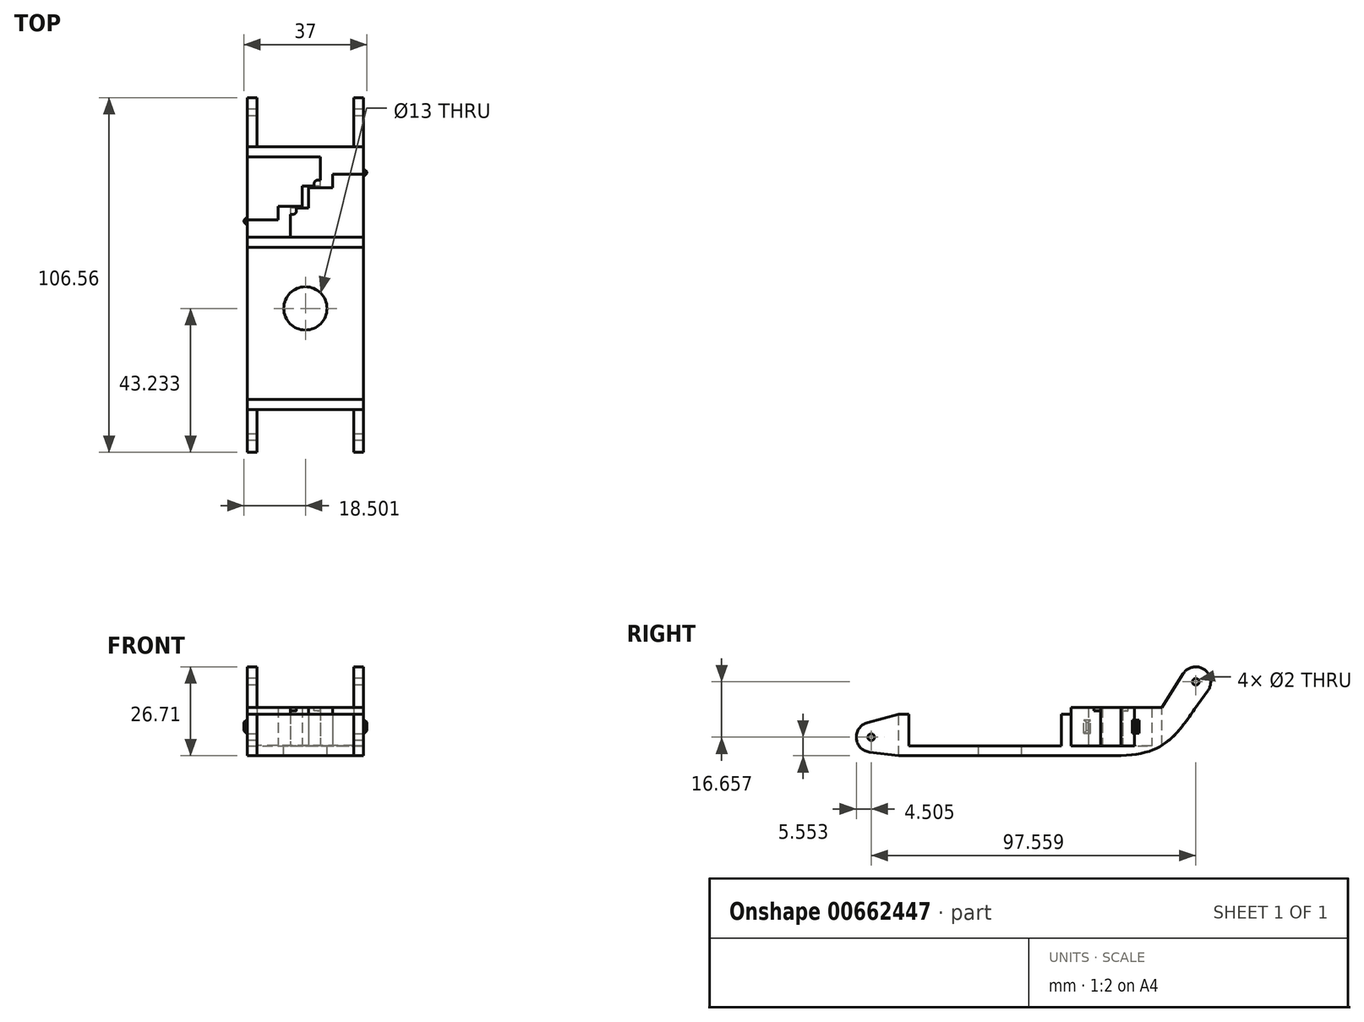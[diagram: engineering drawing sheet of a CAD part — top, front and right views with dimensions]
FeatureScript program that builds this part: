
annotation { "Feature Type Name" : "Feature", "Feature Type Description" : "" }
export const myFeature = defineFeature(function(context is Context, id is Id, definition is map)
    precondition{}
    {
        {
            var Q0;
            Q0=qCreatedBy(makeId("Top.planeOp"),FACE);
            var sketch = newSketch(context, id + "F0", { "sketchPlane" : qUnion([Q0])});
            skLineSegment(sketch, "E0.bottom", {"start": v(-9.64, 16.1) * mm, "end": v(7.86, 16.1) * mm});
            skLineSegment(sketch, "E0.top", {"start": v(-9.64, -29.7) * mm, "end": v(25.36, -29.7) * mm});
            skLineSegment(sketch, "E0.left", {"start": v(-9.64, 16.1) * mm, "end": v(-9.64, -29.7) * mm});
            skLineSegment(sketch, "E1", {"start": v(7.86, 16.1) * mm, "end": v(25.36, 16.1) * mm});
            skCircle(sketch, "E2", {"center": v(7.86, -2.29) * mm, "radius": 6.5 * mm});
            skLineSegment(sketch, "E3.MirrorCS", {"start": v(-9.64, 43.3) * mm, "end": v(-6.47, 43.3) * mm});
            skLineSegment(sketch, "E4.MirrorCS", {"start": v(7.86, 27.9) * mm, "end": v(7.86, 34.5) * mm});
            skLineSegment(sketch, "E5.MirrorCS", {"start": v(-9.64, 24.3) * mm, "end": v(-0.34, 24.3) * mm});
            skLineSegment(sketch, "E6.MirrorCS", {"start": v(12.36, 35.3) * mm, "end": v(12.36, 43.3) * mm});
            skLineSegment(sketch, "E7.MirrorCS", {"start": v(-6.47, 43.3) * mm, "end": v(12.36, 43.3) * mm});
            skLineSegment(sketch, "E8.MirrorCS", {"start": v(-9.64, 24.3) * mm, "end": v(-9.64, 43.3) * mm});
            skPoint(sketch, "E9", {"position": v(7.86, 31.6) * mm});
            skLineSegment(sketch, "E10", {"start": v(-9.64, 16.1) * mm, "end": v(-9.64, 19.1) * mm});
            skLineSegment(sketch, "E11", {"start": v(-9.64, 19.1) * mm, "end": v(25.36, 19.1) * mm});
            skLineSegment(sketch, "E12", {"start": v(-9.64, -29.7) * mm, "end": v(-9.64, -32.7) * mm});
            skLineSegment(sketch, "E13", {"start": v(-9.64, -32.7) * mm, "end": v(25.36, -32.7) * mm});
            skLineSegment(sketch, "E14", {"start": v(25.36, -32.7) * mm, "end": v(25.36, -29.7) * mm});
            skLineSegment(sketch, "E15", {"start": v(25.36, 19.1) * mm, "end": v(25.36, 19.1) * mm});
            skLineSegment(sketch, "E16", {"start": v(25.36, 19.1) * mm, "end": v(25.36, -29.7) * mm});
            skLineSegment(sketch, "E17.MirrorCS", {"start": v(25.36, 19.1) * mm, "end": v(22.2, 19.1) * mm});
            skLineSegment(sketch, "E18.MirrorCS", {"start": v(7.86, 34.5) * mm, "end": v(7.86, 27.9) * mm});
            skLineSegment(sketch, "E19.MirrorCS", {"start": v(25.36, 38.1) * mm, "end": v(16.06, 38.1) * mm});
            skLineSegment(sketch, "E20.MirrorCS", {"start": v(3.36, 27.1) * mm, "end": v(3.36, 19.1) * mm});
            skLineSegment(sketch, "E21.MirrorCS", {"start": v(22.2, 19.1) * mm, "end": v(3.36, 19.1) * mm});
            skLineSegment(sketch, "E22.MirrorCS", {"start": v(25.36, 38.1) * mm, "end": v(25.36, 19.1) * mm});
            skPoint(sketch, "E23", {"position": v(7.86, 30.8) * mm});
            skLineSegment(sketch, "E24", {"start": v(-9.64, 19.1) * mm, "end": v(-9.64, 24.3) * mm});
            skLineSegment(sketch, "E25", {"start": v(12.36, 43.3) * mm, "end": v(25.36, 43.3) * mm});
            skLineSegment(sketch, "E26", {"start": v(25.36, 43.3) * mm, "end": v(25.36, 38.1) * mm});
            skLineSegment(sketch, "E27", {"start": v(-9.64, 43.3) * mm, "end": v(-9.64, 46.3) * mm});
            skLineSegment(sketch, "E28", {"start": v(-9.64, 46.3) * mm, "end": v(25.36, 46.3) * mm});
            skLineSegment(sketch, "E29", {"start": v(25.36, 46.3) * mm, "end": v(25.36, 43.3) * mm});
            skLineSegment(sketch, "E30", {"start": v(25.36, -29.4) * mm, "end": v(-9.64, -29.4) * mm});
            skLineSegment(sketch, "E31", {"start": v(16.06, 38.1) * mm, "end": v(16.06, 34) * mm});
            skLineSegment(sketch, "E32", {"start": v(16.06, 34) * mm, "end": v(7.86, 34) * mm});
            skLineSegment(sketch, "E33", {"start": v(7.86, 34.5) * mm, "end": v(12.36, 34.5) * mm});
            skLineSegment(sketch, "E34", {"start": v(12.36, 34.5) * mm, "end": v(12.36, 35.3) * mm});
            skLineSegment(sketch, "E35", {"start": v(-0.34, 24.3) * mm, "end": v(-0.34, 28.4) * mm});
            skLineSegment(sketch, "E36", {"start": v(7.86, 27.9) * mm, "end": v(3.36, 27.9) * mm});
            skLineSegment(sketch, "E37", {"start": v(3.36, 27.9) * mm, "end": v(3.36, 27.1) * mm});
            skLineSegment(sketch, "E38", {"start": v(7.86, 34.5) * mm, "end": v(6.93, 34.5) * mm});
            skLineSegment(sketch, "E39", {"start": v(7.86, 27.9) * mm, "end": v(8.8, 27.9) * mm});
            skLineSegment(sketch, "E40", {"start": v(6.93, 34.5) * mm, "end": v(6.93, 28.4) * mm});
            skLineSegment(sketch, "E41", {"start": v(8.8, 27.9) * mm, "end": v(8.8, 34) * mm});
            skLineSegment(sketch, "E42", {"start": v(-0.34, 28.4) * mm, "end": v(7.86, 28.4) * mm});
            skSolve(sketch);
        }
        {
            var Q0;
            {var subQ2=sQuery(id+"F0.wireOp",EDGE,"E0.bottom");Q0=makeQuery(id+"F0.imprint","IMPRINT",FACE,{"disambiguationData":[TD([[makeQuery(id+"F0.imprint","IMPRINT",EDGE,{"derivedFrom":subQ2}),-1.0]])]});}
            var Q1;
            Q1=makeQuery(id+"F0.imprint","IMPRINT",FACE,{"disambiguationData":[TD([[makeQuery(id+"F0.imprint","IMPRINT",EDGE,{"derivedFrom":sQuery(id+"F0.wireOp",EDGE,"E0.top")}),-1.0]])]});
            var Q2;
            Q2=makeQuery(id+"F0.imprint","IMPRINT",FACE,{"disambiguationData":[TD([[makeQuery(id+"F0.imprint","IMPRINT",EDGE,{"derivedFrom":sQuery(id+"F0.wireOp",EDGE,"E0.bottom")}),1.0]])]});
            var Q3;
            {var subQ1=sQuery(id+"F0.wireOp",EDGE,"65957815-49e4-4ce0-b1aa-900a07c07509.MirrorCS");Q3=makeQuery(id+"F0.imprint","IMPRINT",FACE,{"disambiguationData":[TD([[makeQuery(id+"F0.imprint","IMPRINT",EDGE,{"derivedFrom":subQ1}),-1.0]])]});}
            var Q4;
            Q4=makeQuery(id+"F0.imprint","IMPRINT",FACE,{"disambiguationData":[TD([[makeQuery(id+"F0.imprint","IMPRINT",EDGE,{"derivedFrom":sQuery(id+"F0.wireOp",EDGE,"793e653a-9070-4513-9301-6aa9de76053a.MirrorCS")}),-1.0]])]});
            var Q5;
            {var subQ3=sQuery(id+"F0.wireOp",EDGE,"bcf4ff58-2fc9-42ac-b040-1ddef6c83d7c.MirrorCS");Q5=makeQuery(id+"F0.imprint","IMPRINT",FACE,{"disambiguationData":[TD([[makeQuery(id+"F0.imprint","IMPRINT",EDGE,{"derivedFrom":subQ3}),1.0]])]});}
            var Q6;
            Q6=makeQuery(id+"F0.imprint","IMPRINT",FACE,{"disambiguationData":[TD([[makeQuery(id+"F0.imprint","IMPRINT",EDGE,{"derivedFrom":sQuery(id+"F0.wireOp",EDGE,"793e653a-9070-4513-9301-6aa9de76053a.MirrorCS")}),1.0]])]});
            var Q7;
            Q7=makeQuery(id+"F0.imprint","IMPRINT",FACE,{"disambiguationData":[TD([[makeQuery(id+"F0.imprint","IMPRINT",EDGE,{"derivedFrom":sQuery(id+"F0.wireOp",EDGE,"E3.MirrorCS")}),1.0]])]});
            var Q8;
            {var subQ0=sQuery(id+"F0.wireOp",EDGE,"E0.top");Q8=makeQuery(id+"F0.imprint","IMPRINT",FACE,{"disambiguationData":[TD([[makeQuery(id+"F0.imprint","IMPRINT",EDGE,{"derivedFrom":subQ0}),1.0]])]});}
            var Q9;
            Q9=makeQuery(id+"F0.imprint","IMPRINT",FACE,{"disambiguationData":[TD([[makeQuery(id+"F0.imprint","IMPRINT",EDGE,{"derivedFrom":sQuery(id+"F0.wireOp",EDGE,"E6.MirrorCS")}),-1.0]])]});
            var Q10;
            Q10=makeQuery(id+"F0.imprint","IMPRINT",FACE,{"disambiguationData":[TD([[makeQuery(id+"F0.imprint","IMPRINT",EDGE,{"derivedFrom":sQuery(id+"F0.wireOp",EDGE,"E5.MirrorCS")}),-1.0]])]});
            var Q11;
            {var subQ3=sQuery(id+"F0.wireOp",EDGE,"E38");Q11=makeQuery(id+"F0.imprint","IMPRINT",FACE,{"disambiguationData":[TD([[makeQuery(id+"F0.imprint","IMPRINT",EDGE,{"derivedFrom":subQ3}),1.0]])]});}
            var Q12;
            {var subQ0=sQuery(id+"F0.wireOp",EDGE,"E39");Q12=makeQuery(id+"F0.imprint","IMPRINT",FACE,{"disambiguationData":[TD([[makeQuery(id+"F0.imprint","IMPRINT",EDGE,{"derivedFrom":subQ0}),1.0]])]});}
            var Q13;
            Q13=makeQuery(id+"F0.imprint","IMPRINT",FACE,{"disambiguationData":[TD([[makeQuery(id+"F0.imprint","IMPRINT",EDGE,{"derivedFrom":sQuery(id+"F0.wireOp",EDGE,"E3.MirrorCS")}),-1.0]])]});
            var Q14;
            Q14=makeQuery(id+"F0.imprint","IMPRINT",FACE,{"disambiguationData":[TD([[makeQuery(id+"F0.imprint","IMPRINT",EDGE,{"derivedFrom":sQuery(id+"F0.wireOp",EDGE,"E19.MirrorCS")}),1.0]])]});
            extrude(context, id + "F1", {"entities" : qUnion([Q0, Q1, Q2, Q3, Q4, Q5, Q6, Q7, Q8, Q9, Q10, Q11, Q12, Q13, Q14]), "oppositeDirection" : true, "depth" : 3 * mm, "offsetDistance" : 25 * mm});
        }
        {
            var Q0;
            Q0=makeQuery(id+"F0.imprint","IMPRINT",FACE,{"disambiguationData":[TD([[makeQuery(id+"F0.imprint","IMPRINT",EDGE,{"derivedFrom":sQuery(id+"F0.wireOp",EDGE,"E0.top")}),-1.0]])]});
            var Q1;
            Q1=makeQuery(id+"F0.imprint","IMPRINT",FACE,{"disambiguationData":[TD([[makeQuery(id+"F0.imprint","IMPRINT",EDGE,{"derivedFrom":sQuery(id+"F0.wireOp",EDGE,"E0.bottom")}),1.0]])]});
            extrude(context, id + "F2", {"entities" : qUnion([Q0, Q1]), "operationType" : NewBodyOperationType.ADD, "depth" : 9.5 * mm, "offsetDistance" : 25 * mm});
        }
        {
            var Q0;
            {var subQ1=sQuery(id+"F0.wireOp",EDGE,"65957815-49e4-4ce0-b1aa-900a07c07509.MirrorCS");Q0=makeQuery(id+"F0.imprint","IMPRINT",FACE,{"disambiguationData":[TD([[makeQuery(id+"F0.imprint","IMPRINT",EDGE,{"derivedFrom":subQ1}),-1.0]])]});}
            var Q1;
            Q1=makeQuery(id+"F0.imprint","IMPRINT",FACE,{"disambiguationData":[TD([[makeQuery(id+"F0.imprint","IMPRINT",EDGE,{"derivedFrom":sQuery(id+"F0.wireOp",EDGE,"793e653a-9070-4513-9301-6aa9de76053a.MirrorCS")}),-1.0]])]});
            var Q2;
            Q2=makeQuery(id+"F0.imprint","IMPRINT",FACE,{"disambiguationData":[TD([[makeQuery(id+"F0.imprint","IMPRINT",EDGE,{"derivedFrom":sQuery(id+"F0.wireOp",EDGE,"E3.MirrorCS")}),1.0]])]});
            var Q3;
            Q3=makeQuery(id+"F0.imprint","IMPRINT",FACE,{"disambiguationData":[TD([[makeQuery(id+"F0.imprint","IMPRINT",EDGE,{"derivedFrom":sQuery(id+"F0.wireOp",EDGE,"E5.MirrorCS")}),-1.0]])]});
            var Q4;
            {var subQ0=sQuery(id+"F0.wireOp",EDGE,"E39");Q4=makeQuery(id+"F0.imprint","IMPRINT",FACE,{"disambiguationData":[TD([[makeQuery(id+"F0.imprint","IMPRINT",EDGE,{"derivedFrom":subQ0}),1.0]])]});}
            var Q5;
            {var subQ3=sQuery(id+"F0.wireOp",EDGE,"E38");Q5=makeQuery(id+"F0.imprint","IMPRINT",FACE,{"disambiguationData":[TD([[makeQuery(id+"F0.imprint","IMPRINT",EDGE,{"derivedFrom":subQ3}),1.0]])]});}
            var Q6;
            Q6=makeQuery(id+"F0.imprint","IMPRINT",FACE,{"disambiguationData":[TD([[makeQuery(id+"F0.imprint","IMPRINT",EDGE,{"derivedFrom":sQuery(id+"F0.wireOp",EDGE,"E6.MirrorCS")}),-1.0]])]});
            extrude(context, id + "F3", {"entities" : qUnion([Q0, Q1, Q2, Q3, Q4, Q5, Q6]), "operationType" : NewBodyOperationType.ADD, "depth" : 11.5 * mm, "offsetDistance" : 25 * mm});
        }
        {
            var Q0;
            {var subQ0=sQuery(id+"F0.wireOp",EDGE,"E29");var subQ1=sQuery(id+"F0.wireOp",EDGE,"E26");var subQ2=sQuery(id+"F0.wireOp",EDGE,"E16");var subQ3=sQuery(id+"F0.wireOp",EDGE,"E14");Q0=makeQuery(id+"F3.boolean.opBoolean","MERGE",FACE,{"derivedFrom":[makeQuery(id+"F2.boolean.opBoolean","MERGE",FACE,{"derivedFrom":[makeQuery(id+"F1.opExtrude","SWEPT_FACE",FACE,{"disambiguationData":[OSD([subQ3,subQ2,sQuery(id+"F0.wireOp",EDGE,"E22.MirrorCS"),subQ1,subQ0])]}),makeQuery(id+"F2.opExtrude","SWEPT_FACE",FACE,{"disambiguationData":[OSD([subQ3])]}),makeQuery(id+"F2.opExtrude","SWEPT_FACE",FACE,{"disambiguationData":[OSD([subQ2])]})]}),makeQuery(id+"F3.opExtrude","SWEPT_FACE",FACE,{"disambiguationData":[OSD([subQ1,subQ0])]})]});}
            var sketch = newSketch(context, id + "F4", { "sketchPlane" : qUnion([Q0])});
            skLineSegment(sketch, "E43.6", {"start": v(46.3, -3) * mm, "end": v(46.3, 11.5) * mm});
            skLineSegment(sketch, "E43.7", {"start": v(46.3, 11.5) * mm, "end": v(38.1, 11.5) * mm});
            skLineSegment(sketch, "E43.8", {"start": v(-32.7, -3) * mm, "end": v(-32.7, 9.5) * mm});
            skCircle(sketch, "E44", {"center": v(56.54, 19.2) * mm, "radius": 4.5 * mm});
            skLineSegment(sketch, "E45", {"start": v(46.3, -3) * mm, "end": v(60.21, 16.6) * mm});
            skLineSegment(sketch, "E46", {"start": v(46.3, 11.5) * mm, "end": v(52.75, 21.63) * mm});
            skCircle(sketch, "E47", {"center": v(-41.02, 2.55) * mm, "radius": 4.5 * mm});
            skLineSegment(sketch, "E48", {"start": v(-32.7, 9.5) * mm, "end": v(-42.2, 6.9) * mm});
            skLineSegment(sketch, "E49", {"start": v(-32.7, -3) * mm, "end": v(-41.56, -1.91) * mm});
            skSolve(sketch);
        }
        {
            var Q0;
            {var subQ0=sQuery(id+"F4.wireOp",EDGE,"E47");var subQ1=makeQuery(id+"F4.imprint","INTERSECT",VERTEX,{"derivedFrom":[subQ0,sQuery(id+"F4.wireOp",EDGE,"PAik2qhj-YHKu-fe6H-CUS2-yW6YpYjkYPtX")]});Q0=makeQuery(id+"F4.imprint","IMPRINT",FACE,{"disambiguationData":[TD([[makeQuery(id+"F4.imprint","IMPRINT",EDGE,{"disambiguationData":[TD([[subQ1,1.0]])],"derivedFrom":subQ0}),1.0]])]});}
            var Q1;
            Q1=makeQuery(id+"F4.imprint","IMPRINT",FACE,{"disambiguationData":[TD([[makeQuery(id+"F4.imprint","IMPRINT",EDGE,{"derivedFrom":sQuery(id+"F4.wireOp",EDGE,"E43.8")}),1.0]])]});
            var Q2;
            Q2=makeQuery(id+"F4.imprint","IMPRINT",FACE,{"disambiguationData":[TD([[makeQuery(id+"F4.imprint","IMPRINT",EDGE,{"derivedFrom":sQuery(id+"F4.wireOp",EDGE,"E43.6")}),-1.0]])]});
            var Q3;
            {var subQ0=sQuery(id+"F4.wireOp",EDGE,"E44");var subQ1=makeQuery(id+"F4.imprint","INTERSECT",VERTEX,{"derivedFrom":[subQ0,sQuery(id+"F4.wireOp",EDGE,"E45")]});Q3=makeQuery(id+"F4.imprint","IMPRINT",FACE,{"disambiguationData":[TD([[makeQuery(id+"F4.imprint","IMPRINT",EDGE,{"disambiguationData":[TD([[subQ1,1.0]])],"derivedFrom":subQ0}),1.0]])]});}
            extrude(context, id + "F5", {"entities" : qUnion([Q0, Q1, Q2, Q3]), "operationType" : NewBodyOperationType.ADD, "oppositeDirection" : true, "depth" : 3 * mm, "offsetDistance" : 25 * mm});
        }
        {
            var Q0;
            {var subQ0=sQuery(id+"F0.wireOp",EDGE,"E27");var subQ1=sQuery(id+"F0.wireOp",EDGE,"E24");var subQ2=sQuery(id+"F0.wireOp",EDGE,"E12");var subQ3=sQuery(id+"F0.wireOp",EDGE,"E10");Q0=makeQuery(id+"F3.boolean.opBoolean","MERGE",FACE,{"derivedFrom":[makeQuery(id+"F2.boolean.opBoolean","MERGE",FACE,{"derivedFrom":[makeQuery(id+"F1.opExtrude","SWEPT_FACE",FACE,{"disambiguationData":[OSD([sQuery(id+"F0.wireOp",EDGE,"E0.left"),sQuery(id+"F0.wireOp",EDGE,"E8.MirrorCS"),subQ3,subQ2,subQ1,subQ0])]}),makeQuery(id+"F2.opExtrude","SWEPT_FACE",FACE,{"disambiguationData":[OSD([subQ3])]}),makeQuery(id+"F2.opExtrude","SWEPT_FACE",FACE,{"disambiguationData":[OSD([subQ2])]})]}),makeQuery(id+"F3.opExtrude","SWEPT_FACE",FACE,{"disambiguationData":[OSD([subQ1])]}),makeQuery(id+"F3.opExtrude","SWEPT_FACE",FACE,{"disambiguationData":[OSD([subQ0])]})]});}
            var sketch = newSketch(context, id + "F6", { "sketchPlane" : qUnion([Q0])});
            skLineSegment(sketch, "E50.0", {"start": v(-46.3, -3) * mm, "end": v(-60.21, 16.6) * mm});
            skArc(sketch, "E50.1", {"start": v(-60.21, 16.6) * mm, "mid": v(-59.06, 22.94) * mm, "end": v(-52.75, 21.63) * mm});
            skLineSegment(sketch, "E50.2", {"start": v(-46.3, 11.5) * mm, "end": v(-52.75, 21.63) * mm});
            skLineSegment(sketch, "E50.3", {"start": v(-46.3, -3) * mm, "end": v(-46.3, 11.5) * mm});
            skLineSegment(sketch, "E50.4", {"start": v(32.7, -3) * mm, "end": v(32.7, 9.5) * mm});
            skLineSegment(sketch, "E50.5", {"start": v(32.7, 9.5) * mm, "end": v(42.2, 6.9) * mm});
            skArc(sketch, "E50.6", {"start": v(42.2, 6.9) * mm, "mid": v(45.5, 2.23) * mm, "end": v(41.56, -1.91) * mm});
            skLineSegment(sketch, "E50.7", {"start": v(32.7, -3) * mm, "end": v(41.56, -1.91) * mm});
            skSolve(sketch);
        }
        {
            var Q0;
            Q0=makeQuery(id+"F6.imprint","IMPRINT",FACE,{"disambiguationData":[TD([[makeQuery(id+"F6.imprint","IMPRINT",EDGE,{"derivedFrom":sQuery(id+"F6.wireOp",EDGE,"E50.0")}),-1.0]])]});
            var Q1;
            Q1=makeQuery(id+"F6.imprint","IMPRINT",FACE,{"disambiguationData":[TD([[makeQuery(id+"F6.imprint","IMPRINT",EDGE,{"derivedFrom":sQuery(id+"F6.wireOp",EDGE,"E50.4")}),-1.0]])]});
            extrude(context, id + "F7", {"entities" : qUnion([Q0, Q1]), "operationType" : NewBodyOperationType.ADD, "oppositeDirection" : true, "depth" : 3 * mm, "offsetDistance" : 25 * mm});
        }
        {
            var Q0;
            {var subQ0=sQuery(id+"F0.wireOp",EDGE,"E27");var subQ1=sQuery(id+"F0.wireOp",EDGE,"E24");var subQ2=sQuery(id+"F0.wireOp",EDGE,"E12");var subQ3=sQuery(id+"F0.wireOp",EDGE,"E10");Q0=makeQuery(id+"F7.boolean.opBoolean","MERGE",FACE,{"derivedFrom":[makeQuery(id+"F3.boolean.opBoolean","MERGE",FACE,{"derivedFrom":[makeQuery(id+"F2.boolean.opBoolean","MERGE",FACE,{"derivedFrom":[makeQuery(id+"F1.opExtrude","SWEPT_FACE",FACE,{"disambiguationData":[OSD([sQuery(id+"F0.wireOp",EDGE,"E0.left"),sQuery(id+"F0.wireOp",EDGE,"E8.MirrorCS"),subQ3,subQ2,subQ1,subQ0])]}),makeQuery(id+"F2.opExtrude","SWEPT_FACE",FACE,{"disambiguationData":[OSD([subQ3])]}),makeQuery(id+"F2.opExtrude","SWEPT_FACE",FACE,{"disambiguationData":[OSD([subQ2])]})]}),makeQuery(id+"F3.opExtrude","SWEPT_FACE",FACE,{"disambiguationData":[OSD([subQ1])]}),makeQuery(id+"F3.opExtrude","SWEPT_FACE",FACE,{"disambiguationData":[OSD([subQ0])]})]}),makeQuery(id+"F7.opExtrude","CAP_FACE",FACE,{"disambiguationData":[OSD([sQuery(id+"F6.wireOp",EDGE,"E50.0"),sQuery(id+"F6.wireOp",EDGE,"E50.1"),sQuery(id+"F6.wireOp",EDGE,"E50.2"),sQuery(id+"F6.wireOp",EDGE,"E50.3")])],"isStart":true}),makeQuery(id+"F7.opExtrude","CAP_FACE",FACE,{"disambiguationData":[OSD([sQuery(id+"F6.wireOp",EDGE,"E50.4"),sQuery(id+"F6.wireOp",EDGE,"E50.5"),sQuery(id+"F6.wireOp",EDGE,"E50.6"),sQuery(id+"F6.wireOp",EDGE,"E50.7")])],"isStart":true})]});}
            var sketch = newSketch(context, id + "F8", { "sketchPlane" : qUnion([Q0])});
            skArc(sketch, "E51.0", {"start": v(-60.21, 16.6) * mm, "mid": v(-59.06, 22.94) * mm, "end": v(-52.75, 21.63) * mm});
            skArc(sketch, "E51.1", {"start": v(42.2, 6.9) * mm, "mid": v(45.5, 2.23) * mm, "end": v(41.56, -1.91) * mm});
            skCircle(sketch, "E52", {"center": v(-56.54, 19.2) * mm, "radius": 1 * mm});
            skCircle(sketch, "E53", {"center": v(41.02, 2.55) * mm, "radius": 1 * mm});
            skSolve(sketch);
        }
        {
            var Q0;
            Q0=makeQuery(id+"F8.imprint","IMPRINT",FACE,{"disambiguationData":[TD([[makeQuery(id+"F8.imprint","IMPRINT",EDGE,{"derivedFrom":sQuery(id+"F8.wireOp",EDGE,"E52")}),1.0]])]});
            var Q1;
            Q1=makeQuery(id+"F8.imprint","IMPRINT",FACE,{"disambiguationData":[TD([[makeQuery(id+"F8.imprint","IMPRINT",EDGE,{"derivedFrom":sQuery(id+"F8.wireOp",EDGE,"E53")}),1.0]])]});
            extrude(context, id + "F9", {"entities" : qUnion([Q0, Q1]), "operationType" : NewBodyOperationType.REMOVE, "endBound" : BoundingType.THROUGH_ALL, "oppositeDirection" : true, "depth" : 25 * mm, "offsetDistance" : 25 * mm});
        }
        {
            var Q0;
            {var subQ0=sQuery(id+"F0.wireOp",EDGE,"E29");var subQ1=sQuery(id+"F0.wireOp",EDGE,"E26");var subQ2=sQuery(id+"F0.wireOp",EDGE,"E16");var subQ3=sQuery(id+"F0.wireOp",EDGE,"E14");Q0=makeQuery(id+"F5.boolean.opBoolean","MERGE",FACE,{"derivedFrom":[makeQuery(id+"F3.boolean.opBoolean","MERGE",FACE,{"derivedFrom":[makeQuery(id+"F2.boolean.opBoolean","MERGE",FACE,{"derivedFrom":[makeQuery(id+"F1.opExtrude","SWEPT_FACE",FACE,{"disambiguationData":[OSD([subQ3,subQ2,sQuery(id+"F0.wireOp",EDGE,"E22.MirrorCS"),subQ1,subQ0])]}),makeQuery(id+"F2.opExtrude","SWEPT_FACE",FACE,{"disambiguationData":[OSD([subQ3])]}),makeQuery(id+"F2.opExtrude","SWEPT_FACE",FACE,{"disambiguationData":[OSD([subQ2])]})]}),makeQuery(id+"F3.opExtrude","SWEPT_FACE",FACE,{"disambiguationData":[OSD([subQ1,subQ0])]})]}),makeQuery(id+"F5.opExtrude","CAP_FACE",FACE,{"disambiguationData":[OSD([sQuery(id+"F4.wireOp",EDGE,"E43.6"),sQuery(id+"F4.wireOp",EDGE,"E44"),sQuery(id+"F4.wireOp",EDGE,"E45"),sQuery(id+"F4.wireOp",EDGE,"E46")])],"isStart":true}),makeQuery(id+"F5.opExtrude","CAP_FACE",FACE,{"disambiguationData":[OSD([sQuery(id+"F4.wireOp",EDGE,"E43.8"),sQuery(id+"F4.wireOp",EDGE,"E47"),sQuery(id+"F4.wireOp",EDGE,"E48"),sQuery(id+"F4.wireOp",EDGE,"E49")])],"isStart":true})]});}
            var sketch = newSketch(context, id + "F10", { "sketchPlane" : qUnion([Q0])});
            skLineSegment(sketch, "E54.0", {"start": v(38.1, 11.5) * mm, "end": v(38.1, 0) * mm});
            skPoint(sketch, "E55", {"position": v(38.1, 5.75) * mm});
            skLineSegment(sketch, "E56", {"start": v(35.03, 5.75) * mm, "end": v(42.1, 5.75) * mm, "construction": true});
            skLineSegment(sketch, "E57", {"start": v(37.5, 5.75) * mm, "end": v(37.5, 7.75) * mm});
            skLineSegment(sketch, "E58", {"start": v(37.5, 7.75) * mm, "end": v(39.5, 7.75) * mm});
            skLineSegment(sketch, "E59", {"start": v(39.5, 7.75) * mm, "end": v(39.5, 5.75) * mm});
            skLineSegment(sketch, "E60.MirrorCS", {"start": v(37.5, 3.75) * mm, "end": v(39.5, 3.75) * mm});
            skLineSegment(sketch, "E61.MirrorCS", {"start": v(37.5, 5.75) * mm, "end": v(37.5, 3.75) * mm});
            skLineSegment(sketch, "E62.MirrorCS", {"start": v(39.5, 3.75) * mm, "end": v(39.5, 5.75) * mm});
            skSolve(sketch);
        }
        {
            var Q0;
            {var subQ4=sQuery(id+"F10.wireOp",EDGE,"E59");Q0=makeQuery(id+"F10.imprint","IMPRINT",FACE,{"disambiguationData":[TD([[makeQuery(id+"F10.imprint","IMPRINT",EDGE,{"derivedFrom":subQ4}),-1.0]])]});}
            var Q1;
            {var subQ5=sQuery(id+"F10.wireOp",EDGE,"E57");Q1=makeQuery(id+"F10.imprint","IMPRINT",FACE,{"disambiguationData":[TD([[makeQuery(id+"F10.imprint","IMPRINT",EDGE,{"derivedFrom":subQ5}),-1.0]])]});}
            extrude(context, id + "F11", {"entities" : qUnion([Q0, Q1]), "operationType" : NewBodyOperationType.ADD, "depth" : 1 * mm, "offsetDistance" : 25 * mm});
        }
        {
            var Q0;
            {var subQ0=sQuery(id+"F0.wireOp",EDGE,"E27");var subQ1=sQuery(id+"F0.wireOp",EDGE,"E24");var subQ2=sQuery(id+"F0.wireOp",EDGE,"E12");var subQ3=sQuery(id+"F0.wireOp",EDGE,"E10");Q0=makeQuery(id+"F7.boolean.opBoolean","MERGE",FACE,{"derivedFrom":[makeQuery(id+"F3.boolean.opBoolean","MERGE",FACE,{"derivedFrom":[makeQuery(id+"F2.boolean.opBoolean","MERGE",FACE,{"derivedFrom":[makeQuery(id+"F1.opExtrude","SWEPT_FACE",FACE,{"disambiguationData":[OSD([sQuery(id+"F0.wireOp",EDGE,"E0.left"),sQuery(id+"F0.wireOp",EDGE,"E8.MirrorCS"),subQ3,subQ2,subQ1,subQ0])]}),makeQuery(id+"F2.opExtrude","SWEPT_FACE",FACE,{"disambiguationData":[OSD([subQ3])]}),makeQuery(id+"F2.opExtrude","SWEPT_FACE",FACE,{"disambiguationData":[OSD([subQ2])]})]}),makeQuery(id+"F3.opExtrude","SWEPT_FACE",FACE,{"disambiguationData":[OSD([subQ1])]}),makeQuery(id+"F3.opExtrude","SWEPT_FACE",FACE,{"disambiguationData":[OSD([subQ0])]})]}),makeQuery(id+"F7.opExtrude","CAP_FACE",FACE,{"disambiguationData":[OSD([sQuery(id+"F6.wireOp",EDGE,"E50.0"),sQuery(id+"F6.wireOp",EDGE,"E50.1"),sQuery(id+"F6.wireOp",EDGE,"E50.2"),sQuery(id+"F6.wireOp",EDGE,"E50.3")])],"isStart":true}),makeQuery(id+"F7.opExtrude","CAP_FACE",FACE,{"disambiguationData":[OSD([sQuery(id+"F6.wireOp",EDGE,"E50.4"),sQuery(id+"F6.wireOp",EDGE,"E50.5"),sQuery(id+"F6.wireOp",EDGE,"E50.6"),sQuery(id+"F6.wireOp",EDGE,"E50.7")])],"isStart":true})]});}
            var sketch = newSketch(context, id + "F12", { "sketchPlane" : qUnion([Q0])});
            skLineSegment(sketch, "E63", {"start": v(-24.3, 5.75) * mm, "end": v(-30.81, 5.75) * mm, "construction": true});
            skLineSegment(sketch, "E64", {"start": v(-24.9, 5.75) * mm, "end": v(-24.9, 7.75) * mm});
            skLineSegment(sketch, "E65", {"start": v(-24.9, 7.75) * mm, "end": v(-22.9, 7.75) * mm});
            skLineSegment(sketch, "E66", {"start": v(-22.9, 7.75) * mm, "end": v(-22.9, 5.75) * mm});
            skLineSegment(sketch, "E67.MirrorCS", {"start": v(-24.9, 5.75) * mm, "end": v(-24.9, 3.75) * mm});
            skLineSegment(sketch, "E68.MirrorCS", {"start": v(-22.9, 3.75) * mm, "end": v(-22.9, 5.75) * mm});
            skLineSegment(sketch, "E69.MirrorCS", {"start": v(-24.9, 3.75) * mm, "end": v(-22.9, 3.75) * mm});
            skSolve(sketch);
        }
        {
            var Q0;
            {var subQ1=sQuery(id+"F12.wireOp",EDGE,"E66");Q0=makeQuery(id+"F12.imprint","IMPRINT",FACE,{"disambiguationData":[TD([[makeQuery(id+"F12.imprint","IMPRINT",EDGE,{"derivedFrom":subQ1}),-1.0]])]});}
            var Q1;
            {var subQ5=sQuery(id+"F12.wireOp",EDGE,"E64");Q1=makeQuery(id+"F12.imprint","IMPRINT",FACE,{"disambiguationData":[TD([[makeQuery(id+"F12.imprint","IMPRINT",EDGE,{"derivedFrom":subQ5}),-1.0]])]});}
            extrude(context, id + "F13", {"entities" : qUnion([Q0, Q1]), "operationType" : NewBodyOperationType.ADD, "depth" : 1 * mm, "offsetDistance" : 25 * mm});
        }
        {
            var Q0;
            Q0=makeQuery(id+"F13.opExtrude","CAP_EDGE",EDGE,{"disambiguationData":[OSD([sQuery(id+"F12.wireOp",EDGE,"E64"),sQuery(id+"F12.wireOp",EDGE,"E67.MirrorCS")])],"isStart":false});
            var Q1;
            Q1=makeQuery(id+"F13.opExtrude","CAP_EDGE",EDGE,{"disambiguationData":[OSD([sQuery(id+"F12.wireOp",EDGE,"E66"),sQuery(id+"F12.wireOp",EDGE,"E68.MirrorCS")])],"isStart":false});
            var Q2;
            Q2=makeQuery(id+"F13.opExtrude","CAP_EDGE",EDGE,{"disambiguationData":[OSD([sQuery(id+"F12.wireOp",EDGE,"E65")])],"isStart":false});
            var Q3;
            Q3=makeQuery(id+"F13.opExtrude","CAP_EDGE",EDGE,{"disambiguationData":[OSD([sQuery(id+"F12.wireOp",EDGE,"E69.MirrorCS")])],"isStart":false});
            var Q4;
            Q4=makeQuery(id+"F11.opExtrude","CAP_EDGE",EDGE,{"disambiguationData":[OSD([sQuery(id+"F10.wireOp",EDGE,"E58")])],"isStart":false});
            var Q5;
            Q5=makeQuery(id+"F11.opExtrude","CAP_EDGE",EDGE,{"disambiguationData":[OSD([sQuery(id+"F10.wireOp",EDGE,"E57"),sQuery(id+"F10.wireOp",EDGE,"E61.MirrorCS")])],"isStart":false});
            var Q6;
            Q6=makeQuery(id+"F11.opExtrude","CAP_EDGE",EDGE,{"disambiguationData":[OSD([sQuery(id+"F10.wireOp",EDGE,"E60.MirrorCS")])],"isStart":false});
            var Q7;
            Q7=makeQuery(id+"F11.opExtrude","CAP_EDGE",EDGE,{"disambiguationData":[OSD([sQuery(id+"F10.wireOp",EDGE,"E59"),sQuery(id+"F10.wireOp",EDGE,"E62.MirrorCS")])],"isStart":false});
            chamfer(context, id + "F14", {"entities" : qUnion([Q0, Q1, Q2, Q3, Q4, Q5, Q6, Q7]), "width" : .75 * mm, "tangentPropagation" : true});
        }
        {
            var Q0;
            Q0=makeQuery(id+"F3.opExtrude","CAP_FACE",FACE,{"disambiguationData":[OSD([sQuery(id+"F0.wireOp",EDGE,"E3.MirrorCS"),sQuery(id+"F0.wireOp",EDGE,"E5.MirrorCS"),sQuery(id+"F0.wireOp",EDGE,"E6.MirrorCS"),sQuery(id+"F0.wireOp",EDGE,"E7.MirrorCS"),sQuery(id+"F0.wireOp",EDGE,"E11"),sQuery(id+"F0.wireOp",EDGE,"E19.MirrorCS"),sQuery(id+"F0.wireOp",EDGE,"E20.MirrorCS"),sQuery(id+"F0.wireOp",EDGE,"E24"),sQuery(id+"F0.wireOp",EDGE,"E26"),sQuery(id+"F0.wireOp",EDGE,"E27"),sQuery(id+"F0.wireOp",EDGE,"E28"),sQuery(id+"F0.wireOp",EDGE,"E29"),sQuery(id+"F0.wireOp",EDGE,"E31"),sQuery(id+"F0.wireOp",EDGE,"E32"),sQuery(id+"F0.wireOp",EDGE,"E33"),sQuery(id+"F0.wireOp",EDGE,"E34"),sQuery(id+"F0.wireOp",EDGE,"E35"),sQuery(id+"F0.wireOp",EDGE,"E36"),sQuery(id+"F0.wireOp",EDGE,"E37"),sQuery(id+"F0.wireOp",EDGE,"E38"),sQuery(id+"F0.wireOp",EDGE,"E39"),sQuery(id+"F0.wireOp",EDGE,"E40"),sQuery(id+"F0.wireOp",EDGE,"E41"),sQuery(id+"F0.wireOp",EDGE,"E42")])],"isStart":false});
            var sketch = newSketch(context, id + "F15", { "sketchPlane" : qUnion([Q0])});
            skLineSegment(sketch, "E70.0", {"start": v(12.36, 34.5) * mm, "end": v(6.93, 34.5) * mm});
            skLineSegment(sketch, "E70.1", {"start": v(8.8, 27.9) * mm, "end": v(3.36, 27.9) * mm});
            skLineSegment(sketch, "E71", {"start": v(5.12, 27.9) * mm, "end": v(5.12, 25.96) * mm});
            skPoint(sketch, "E71.endSnap0", {"position": v(3.36, 25.96) * mm});
            skLineSegment(sketch, "E72", {"start": v(5.12, 25.96) * mm, "end": v(3.36, 25.96) * mm});
            skLineSegment(sketch, "E73", {"start": v(3.36, 27.9) * mm, "end": v(3.36, 25.96) * mm});
            skLineSegment(sketch, "E74", {"start": v(10.48, 34.5) * mm, "end": v(10.48, 36.23) * mm});
            skPoint(sketch, "E74.endSnap0", {"position": v(12.36, 36.23) * mm});
            skLineSegment(sketch, "E75", {"start": v(10.48, 36.23) * mm, "end": v(12.36, 36.23) * mm});
            skSolve(sketch);
        }
        {
            var Q0;
            {var subQ3=sQuery(id+"F15.wireOp",EDGE,"E74");Q0=makeQuery(id+"F15.imprint","IMPRINT",FACE,{"disambiguationData":[TD([[makeQuery(id+"F15.imprint","IMPRINT",EDGE,{"derivedFrom":subQ3}),-1.0]])]});}
            var Q1;
            {var subQ2=sQuery(id+"F15.wireOp",EDGE,"E71");Q1=makeQuery(id+"F15.imprint","IMPRINT",FACE,{"disambiguationData":[TD([[makeQuery(id+"F15.imprint","IMPRINT",EDGE,{"derivedFrom":subQ2}),-1.0]])]});}
            extrude(context, id + "F16", {"entities" : qUnion([Q0, Q1]), "operationType" : NewBodyOperationType.ADD, "oppositeDirection" : true, "depth" : 1 * mm, "offsetDistance" : 25 * mm});
        }
        {
            var Q0;
            {var subQ0=sQuery(id+"F0.wireOp",EDGE,"E27");var subQ1=sQuery(id+"F0.wireOp",EDGE,"E24");var subQ2=sQuery(id+"F0.wireOp",EDGE,"E12");var subQ3=sQuery(id+"F0.wireOp",EDGE,"E10");Q0=makeQuery(id+"F7.boolean.opBoolean","MERGE",FACE,{"derivedFrom":[makeQuery(id+"F3.boolean.opBoolean","MERGE",FACE,{"derivedFrom":[makeQuery(id+"F2.boolean.opBoolean","MERGE",FACE,{"derivedFrom":[makeQuery(id+"F1.opExtrude","SWEPT_FACE",FACE,{"disambiguationData":[OSD([sQuery(id+"F0.wireOp",EDGE,"E0.left"),sQuery(id+"F0.wireOp",EDGE,"E8.MirrorCS"),subQ3,subQ2,subQ1,subQ0])]}),makeQuery(id+"F2.opExtrude","SWEPT_FACE",FACE,{"disambiguationData":[OSD([subQ3])]}),makeQuery(id+"F2.opExtrude","SWEPT_FACE",FACE,{"disambiguationData":[OSD([subQ2])]})]}),makeQuery(id+"F3.opExtrude","SWEPT_FACE",FACE,{"disambiguationData":[OSD([subQ1])]}),makeQuery(id+"F3.opExtrude","SWEPT_FACE",FACE,{"disambiguationData":[OSD([subQ0])]})]}),makeQuery(id+"F7.opExtrude","CAP_FACE",FACE,{"disambiguationData":[OSD([sQuery(id+"F6.wireOp",EDGE,"E50.0"),sQuery(id+"F6.wireOp",EDGE,"E50.1"),sQuery(id+"F6.wireOp",EDGE,"E50.2"),sQuery(id+"F6.wireOp",EDGE,"E50.3")])],"isStart":true}),makeQuery(id+"F7.opExtrude","CAP_FACE",FACE,{"disambiguationData":[OSD([sQuery(id+"F6.wireOp",EDGE,"E50.4"),sQuery(id+"F6.wireOp",EDGE,"E50.5"),sQuery(id+"F6.wireOp",EDGE,"E50.6"),sQuery(id+"F6.wireOp",EDGE,"E50.7")])],"isStart":true})]});}
            var sketch = newSketch(context, id + "F17", { "sketchPlane" : qUnion([Q0])});
            skLineSegment(sketch, "E76.0", {"start": v(-46.3, -3) * mm, "end": v(-60.21, 16.6) * mm});
            skLineSegment(sketch, "E76.1", {"start": v(-46.3, -3) * mm, "end": v(32.7, -3) * mm});
            skFitSpline(sketch, "E77", {"points": [v(-56.2, 10.95) * mm, v(-32.24, -3) * mm], "startDerivative": vector(19.25, -27.12) * mm, "endDerivative": vector(42.2, 0) * mm});
            skSolve(sketch);
        }
        {
            var Q0;
            {var subQ3=sQuery(id+"F17.wireOp",EDGE,"E77");Q0=makeQuery(id+"F17.imprint","IMPRINT",FACE,{"disambiguationData":[TD([[makeQuery(id+"F17.imprint","IMPRINT",EDGE,{"derivedFrom":subQ3}),-1.0]])]});}
            extrude(context, id + "F18", {"entities" : qUnion([Q0]), "operationType" : NewBodyOperationType.REMOVE, "endBound" : BoundingType.THROUGH_ALL, "oppositeDirection" : true, "depth" : 25 * mm, "offsetDistance" : 25 * mm});
        }
        {
            var Q0;
            Q0=makeQuery(id+"F16.opExtrude","SWEPT_EDGE",EDGE,{"disambiguationData":[OSD([sQuery(id+"F15.wireOp",EDGE,"E71"),sQuery(id+"F15.wireOp",EDGE,"E72")])]});
            var Q1;
            Q1=makeQuery(id+"F16.opExtrude","SWEPT_EDGE",EDGE,{"disambiguationData":[OSD([sQuery(id+"F15.wireOp",EDGE,"E74"),sQuery(id+"F15.wireOp",EDGE,"E75")])]});
            fillet(context, id + "F19", {"entities" : qUnion([Q0, Q1]), "radius" : 1 * mm, "tangentPropagation" : true, "allowEdgeOverflow" : false});
        }
    });
